FCSTD DOCUMENT  (FreeCAD 0.15R4671 (Git))
Label: Base Plate
License: All rights reserved
LicenseURL: http://en.wikipedia.org/wiki/All_rights_reserved
objects: Sketcher::SketchObject×1
note: 1 computed .brp shape members not serialized (recipe doc carries the construction recipe); baked Part::Feature solids carry a one-line shape summary decoded from their .brp

FEATURE [Sketcher::SketchObject] Sketch
  sketch-geometry (8):
    g0: LineSegment StartX=-100 StartY=35 StartZ=0 EndX=-100 EndY=-35 EndZ=0
    g1: LineSegment StartX=-100 StartY=-35 StartZ=0 EndX=0 EndY=-35 EndZ=0
    g2: LineSegment StartX=0 StartY=-35 StartZ=0 EndX=0 EndY=-70 EndZ=0
    g3: LineSegment StartX=0 StartY=-70 StartZ=0 EndX=50 EndY=-70 EndZ=0
    g4: LineSegment StartX=50 StartY=-70 StartZ=0 EndX=50 EndY=70 EndZ=0
    g5: LineSegment StartX=50 StartY=70 StartZ=0 EndX=0 EndY=70 EndZ=0
    g6: LineSegment StartX=0 StartY=70 StartZ=0 EndX=0 EndY=35 EndZ=0
    g7: LineSegment StartX=0 StartY=35 StartZ=0 EndX=-100 EndY=35 EndZ=0
  constraints (25):
    c: Vertical(g0)
    c: Coincident(g0,g1)
    c: Horizontal(g1)
    c: Coincident(g1,g2)
    c: Vertical(g2)
    c: Coincident(g2,g3)
    c: Coincident(g3,g4)
    c: Vertical(g4)
    c: Coincident(g4,g5)
    c: Horizontal(g5)
    c: Coincident(g5,g6)
    c: Vertical(g6)
    c: Coincident(g6,g7)
    c: PointOnObject(g7,g0)
    c: Horizontal(g7)
    c: Equal(g5,g3)
    c: Equal(g6,g2)
    c: Coincident(g0,g7)
    c: Symmetric(g0,g0,g-1)
    c: Symmetric(g4,g3,g-1)
    c: DistanceY(g4) = 140
    c: DistanceX(g3) = 50
    c: DistanceX(g3,g0) = -150
    c: DistanceY(g0) = -70
    c: PointOnObject(g6,g-2)
